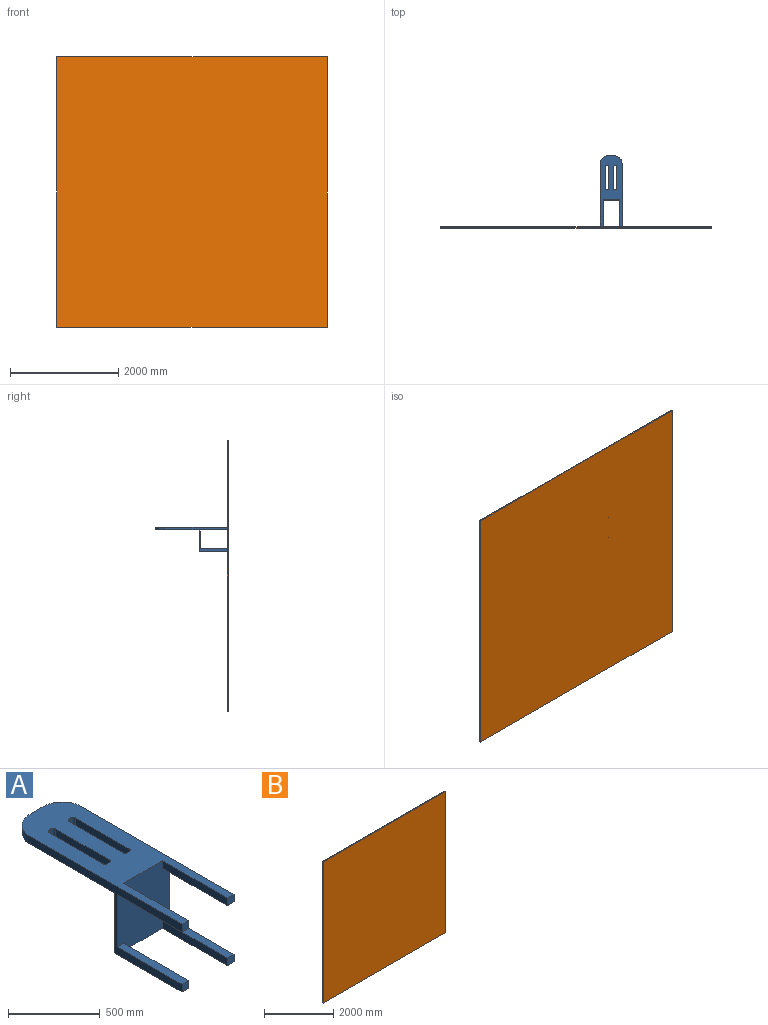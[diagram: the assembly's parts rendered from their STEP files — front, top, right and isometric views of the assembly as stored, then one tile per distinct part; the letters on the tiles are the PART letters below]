
ASSEMBLY  parts=2 mates=1
PART A: 38 faces, bbox 400x1320x450 mm
  f0: plane 1320x400mm, normal (0,0,1), area 324029.6mm2, adj f3,f4,f6,f8,f9,f11,f12,f19
  f1: plane 800x400mm, normal (0,0,-1), area 266029.6mm2, adj f2,f4,f6,f19,f20,f21,f22,f23
  f2: plane 400x400mm, normal (0,1,0), area 160000mm2, adj f1,f4,f5,f6
  f3: plane 450x400mm, normal (0,-1,0), area 170000mm2, adj f0,f4,f5,f6,f7,f8,f10,f11
  f4: plane 1170x450mm, normal (-1,0,0), area 91500mm2, adj f0,f1,f2,f3,f5,f7,f9,f13
  f5: plane 520x400mm, normal (0,0,-1), area 58000mm2, adj f2,f3,f4,f6,f14,f15,f17,f18
  f6: plane 1170x450mm, normal (1,0,0), area 91500mm2, adj f0,f1,f2,f3,f5,f10,f12,f16
  f7: plane 500x50mm, normal (0,0,-1), area 25000mm2, adj f3,f4,f8,f9
  f8: plane 500x50mm, normal (1,0,0), area 25000mm2, adj f0,f3,f7,f9
  f9: plane 50x50mm, normal (0,-1,0), area 2500mm2, adj f0,f4,f7,f8
  f10: plane 500x50mm, normal (0,0,-1), area 25000mm2, adj f3,f6,f11,f12
  f11: plane 500x50mm, normal (-1,0,0), area 25000mm2, adj f0,f3,f10,f12
  f12: plane 50x50mm, normal (0,-1,0), area 2500mm2, adj f0,f6,f10,f11
  f13: plane 500x50mm, normal (0,0,1), area 25000mm2, adj f3,f4,f14,f15
  f14: plane 500x50mm, normal (1,0,0), area 25000mm2, adj f3,f5,f13,f15
  f15: plane 50x50mm, normal (0,-1,0), area 2500mm2, adj f4,f5,f13,f14
  f16: plane 500x50mm, normal (0,0,1), area 25000mm2, adj f3,f6,f17,f18
  f17: plane 500x50mm, normal (-1,0,0), area 25000mm2, adj f3,f5,f16,f18
  f18: plane 50x50mm, normal (0,-1,0), area 2500mm2, adj f5,f6,f16,f17
  f19: plane 100x50mm, normal (0,1,0), area 5000mm2, adj f0,f1,f36,f37
  f20: plane 50x10mm, normal (0,-1,0), area 500mm2, adj f0,f1,f28,f31
  f21: plane 410x50mm, normal (-1,0,0), area 20500mm2, adj f0,f1,f28,f29
  f22: plane 50x10mm, normal (0,1,0), area 500mm2, adj f0,f1,f29,f30
  f23: plane 410x50mm, normal (1,0,0), area 20500mm2, adj f0,f1,f30,f31
  f24: plane 50x10mm, normal (0,-1,0), area 500mm2, adj f0,f1,f32,f35
  f25: plane 410x50mm, normal (-1,0,0), area 20500mm2, adj f0,f1,f34,f35
  f26: plane 50x10mm, normal (0,1,0), area 500mm2, adj f0,f1,f33,f34
  f27: plane 410x50mm, normal (1,0,0), area 20500mm2, adj f0,f1,f32,f33
  f28: cylinder r=20mm len=50mm, axis (0,0,-1), area 1570.8mm2, adj f0,f1,f20,f21
  f29: cylinder r=20mm len=50mm, axis (0,0,1), area 1570.8mm2, adj f0,f1,f21,f22
  f30: cylinder r=20mm len=50mm, axis (0,0,-1), area 1570.8mm2, adj f0,f1,f22,f23
  f31: cylinder r=20mm len=50mm, axis (0,0,1), area 1570.8mm2, adj f0,f1,f20,f23
  f32: cylinder r=20mm len=50mm, axis (0,0,1), area 1570.8mm2, adj f0,f1,f24,f27
  f33: cylinder r=20mm len=50mm, axis (0,0,-1), area 1570.8mm2, adj f0,f1,f26,f27
  f34: cylinder r=20mm len=50mm, axis (0,0,1), area 1570.8mm2, adj f0,f1,f25,f26
  f35: cylinder r=20mm len=50mm, axis (0,0,-1), area 1570.8mm2, adj f0,f1,f24,f25
  f36: cylinder r=150mm len=150mm, axis (0,0,1), area 11781mm2, adj f0,f1,f4,f19
  f37: cylinder r=150mm len=150mm, axis (0,0,-1), area 11781mm2, adj f0,f1,f6,f19
PART B: 6 faces, bbox 5000x20x5000 mm
  f0: plane 5000x20mm, normal (0,0,1), area 100000mm2, adj f1,f3,f4,f5
  f1: plane 5000x20mm, normal (-1,0,0), area 100000mm2, adj f0,f2,f4,f5
  f2: plane 5000x20mm, normal (0,0,-1), area 100000mm2, adj f1,f3,f4,f5
  f3: plane 5000x20mm, normal (1,0,0), area 100000mm2, adj f0,f2,f4,f5
  f4: plane 5000x5000mm, normal (0,-1,0), area 25000000mm2, adj f0,f1,f2,f3
  f5: plane 5000x5000mm, normal (0,1,0), area 25000000mm2, adj f0,f1,f2,f3
PLACE A rot(axis=(-0.88,-0.18,0.44),0deg) t=(1598.75,1334.3,-70.97)mm
PLACE B rot(axis=(-0.88,-0.18,0.44),0deg) t=(951.89,814.3,-515.13)mm
MATE fastened A.f15 <-> B.f5  axis (0,-1,0) through (1450.97,814.3,-183.31)mm
